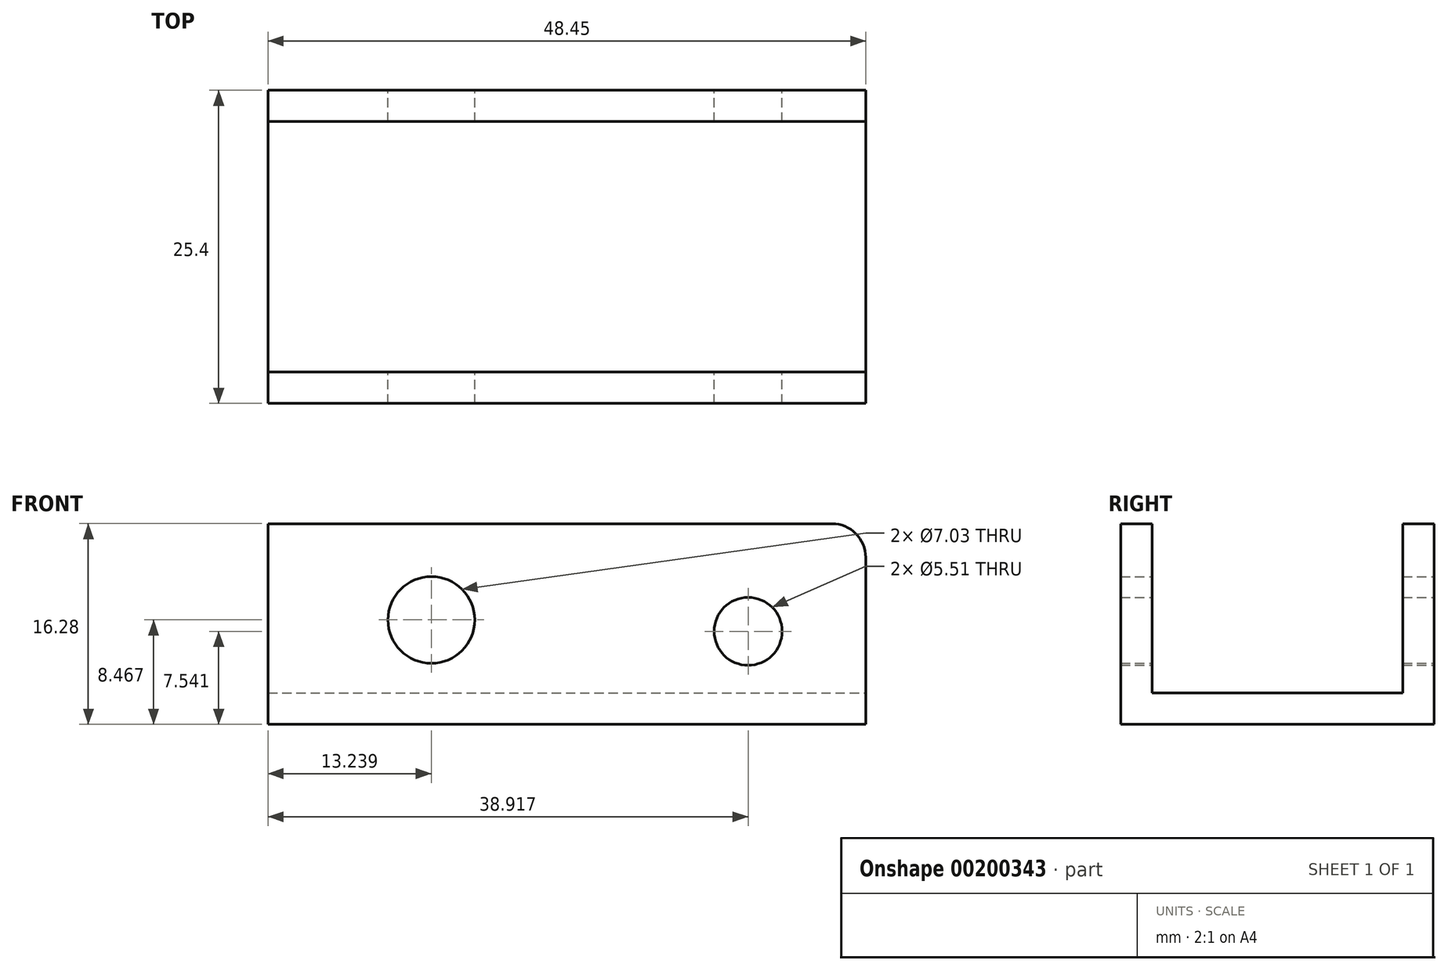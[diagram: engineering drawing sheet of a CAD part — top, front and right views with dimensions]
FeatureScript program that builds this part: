
annotation { "Feature Type Name" : "Feature", "Feature Type Description" : "" }
export const myFeature = defineFeature(function(context is Context, id is Id, definition is map)
    precondition{}
    {
        {
            var Q0;
            Q0=qCreatedBy(makeId("Front.planeOp"),FACE);
            var sketch = newSketch(context, id + "F0", { "sketchPlane" : qUnion([Q0])});
            skLineSegment(sketch, "E0", {"start": v(-66.05, 6.82) * mm, "end": v(-17.6, 6.82) * mm});
            skLineSegment(sketch, "E1", {"start": v(-17.6, 6.82) * mm, "end": v(-17.6, 20.35) * mm});
            skLineSegment(sketch, "E2", {"start": v(-66.05, 6.82) * mm, "end": v(-66.05, 23.1) * mm});
            skPoint(sketch, "E3.end.orphan", {"position": v(-64.99, 23.1) * mm});
            skLineSegment(sketch, "E4", {"start": v(-64.99, 23.1) * mm, "end": v(-66.05, 23.1) * mm});
            skLineSegment(sketch, "E5", {"start": v(-66.05, 23.1) * mm, "end": v(-20.35, 23.1) * mm});
            skPoint(sketch, "E6.visualSharp", {"position": v(-17.6, 23.1) * mm});
            skArc(sketch, "E6.filletArc", {"start": v(-17.6, 20.35) * mm, "mid": v(-18.4, 22.3) * mm, "end": v(-20.35, 23.1) * mm});
            skSolve(sketch);
        }
        {
            var Q0;
            Q0=makeQuery(id+"F0.imprint","IMPRINT",FACE,{"disambiguationData":[TD([[makeQuery(id+"F0.imprint","IMPRINT",EDGE,{"derivedFrom":sQuery(id+"F0.wireOp",EDGE,"E0")}),1.0]])]});
            extrude(context, id + "F1", {"entities" : qUnion([Q0]), "depth" : 25.4 * mm});
        }
        {
            var Q0;
            Q0=makeQuery(id+"F1.opExtrude","SWEPT_FACE",FACE,{"disambiguationData":[OSD([sQuery(id+"F0.wireOp",EDGE,"E5")])]});
            var Q1;
            Q1=makeQuery(id+"F1.opExtrude","SWEPT_FACE",FACE,{"disambiguationData":[OSD([sQuery(id+"F0.wireOp",EDGE,"E1")])]});
            var Q2;
            Q2=makeQuery(id+"F1.opExtrude","SWEPT_FACE",FACE,{"disambiguationData":[OSD([sQuery(id+"F0.wireOp",EDGE,"E6.filletArc")])]});
            var Q3;
            Q3=makeQuery(id+"F1.opExtrude","SWEPT_FACE",FACE,{"disambiguationData":[OSD([sQuery(id+"F0.wireOp",EDGE,"E2")])]});
            shell(context, id + "F2", {"entities" : qUnion([Q0, Q1, Q2, Q3]), "thickness" : 2.54 * mm});
        }
        {
            var Q0;
            Q0=qCreatedBy(makeId("Front.planeOp"),FACE);
            var sketch = newSketch(context, id + "F3", { "sketchPlane" : qUnion([Q0])});
            skCircle(sketch, "E7", {"center": v(-27.13, 14.36) * mm, "radius": 2.75 * mm});
            skCircle(sketch, "E8", {"center": v(-52.81, 15.29) * mm, "radius": 3.52 * mm});
            skSolve(sketch);
        }
        {
            var Q0;
            Q0=makeQuery(id+"F3.imprint","IMPRINT",FACE,{"disambiguationData":[TD([[makeQuery(id+"F3.imprint","IMPRINT",EDGE,{"derivedFrom":sQuery(id+"F3.wireOp",EDGE,"E7")}),1.0]])]});
            var Q1;
            Q1=makeQuery(id+"F3.imprint","IMPRINT",FACE,{"disambiguationData":[TD([[makeQuery(id+"F3.imprint","IMPRINT",EDGE,{"derivedFrom":sQuery(id+"F3.wireOp",EDGE,"E8")}),1.0]])]});
            var Q2;
            Q2=makeQuery(id+"F1.opExtrude","CAP_FACE",FACE,{"disambiguationData":[OSD([sQuery(id+"F0.wireOp",EDGE,"E0"),sQuery(id+"F0.wireOp",EDGE,"E1"),sQuery(id+"F0.wireOp",EDGE,"E2"),sQuery(id+"F0.wireOp",EDGE,"E5"),sQuery(id+"F0.wireOp",EDGE,"E6.filletArc")])],"isStart":false});
            extrude(context, id + "F4", {"entities" : qUnion([Q0, Q1, Q2]), "operationType" : NewBodyOperationType.REMOVE, "depth" : 59.18 * mm});
        }
    });
